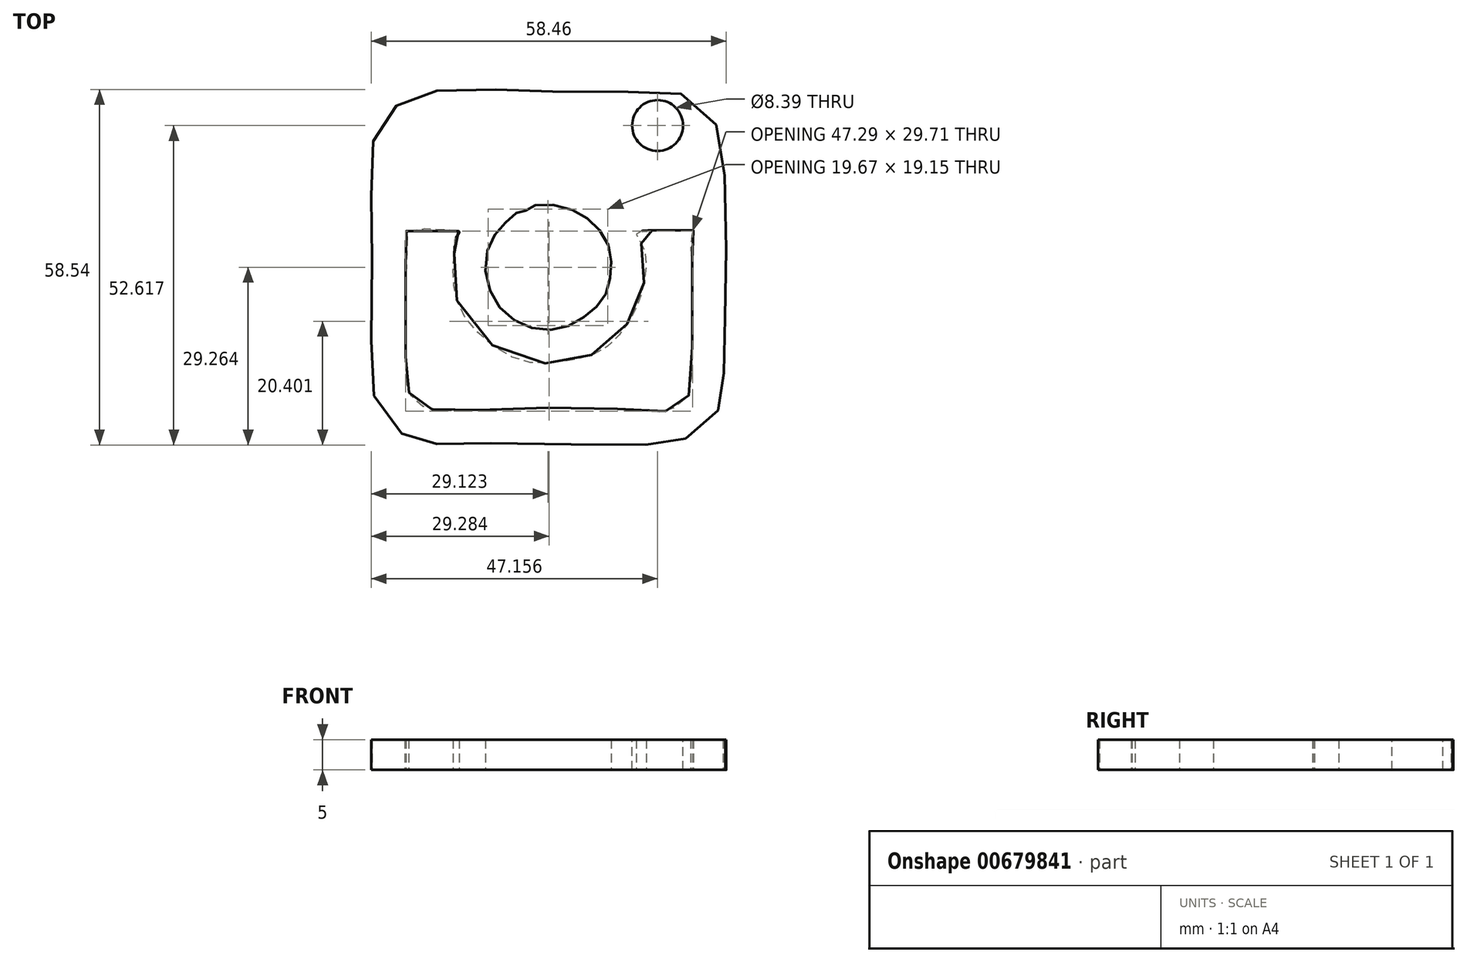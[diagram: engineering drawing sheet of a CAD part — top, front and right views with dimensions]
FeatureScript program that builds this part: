
annotation { "Feature Type Name" : "Feature", "Feature Type Description" : "" }
export const myFeature = defineFeature(function(context is Context, id is Id, definition is map)
    precondition{}
    {
        {
            var Q0;
            Q0=qCreatedBy(makeId("Top.planeOp"),FACE);
            var sketch = newSketch(context, id + "F0", { "sketchPlane" : qUnion([Q0])});
            skFitSpline(sketch, "E0", {"points": [v(-41.99, 61.02) * mm, v(-51.6, 60.82) * mm, v(-56.45, 59.73) * mm, v(-61, 55.57) * mm, v(-62.29, 51.5) * mm, v(-62.49, 42.4) * mm, v(-62.39, 30.61) * mm, v(-62.49, 14.08) * mm, v(-61.6, 9.52) * mm, v(-57.44, 4.37) * mm, v(-53.87, 2.79) * mm, v(-49.71, 2.69) * mm, v(-38.62, 2.79) * mm, v(-20.4, 2.5) * mm, v(-12.88, 2.89) * mm, v(-10.2, 3.88) * mm, v(-6.04, 7.34) * mm, v(-4.26, 11.6) * mm, v(-4.56, 15.56) * mm, v(-4.16, 25.47) * mm, v(-4.16, 38.93) * mm, v(-4.75, 52) * mm, v(-6.44, 56.26) * mm, v(-11.49, 60.32) * mm, v(-18.32, 60.72) * mm, v(-33.37, 60.72) * mm, v(-41.99, 61.02) * mm]});
            skFitSpline(sketch, "E1", {"points": [v(-37.14, 41.11) * mm, v(-38.42, 40.81) * mm, v(-40.8, 38.74) * mm, v(-43.18, 35.27) * mm, v(-43.38, 29.23) * mm, v(-40.5, 24.28) * mm, v(-35.65, 21.7) * mm, v(-30.4, 22) * mm, v(-26.44, 24.38) * mm, v(-23.97, 27.25) * mm, v(-23.07, 31.3) * mm, v(-23.47, 35.37) * mm, v(-26.14, 39.13) * mm, v(-30, 41.4) * mm, v(-35.45, 42) * mm, v(-37.14, 41.11) * mm]});
            skFitSpline(sketch, "E2", {"points": [v(-48.13, 37.74) * mm, v(-56.74, 37.74) * mm, v(-56.55, 37.55) * mm, v(-56.74, 33.59) * mm, v(-56.74, 13.68) * mm, v(-56.55, 11.8) * mm, v(-55.56, 10.12) * mm, v(-53.38, 8.63) * mm, v(-49.32, 8.14) * mm, v(-37.14, 8.53) * mm, v(-21.99, 8.43) * mm, v(-14.36, 8.04) * mm, v(-12.68, 8.63) * mm, v(-10.3, 10.61) * mm, v(-9.8, 13.38) * mm, v(-9.7, 33.39) * mm, v(-9.8, 37.25) * mm, v(-9.5, 37.84) * mm, v(-12.08, 37.84) * mm, v(-18.72, 37.55) * mm, v(-18.82, 36.95) * mm, v(-17.53, 34.67) * mm, v(-17.63, 29.23) * mm, v(-19.6, 23.68) * mm, v(-24.36, 18.24) * mm, v(-30.4, 16.35) * mm, v(-38.23, 16.55) * mm, v(-47.14, 23.68) * mm, v(-49.02, 30.61) * mm, v(-48.72, 35.86) * mm, v(-48.52, 36.75) * mm, v(-48.13, 37.74) * mm]});
            skSolve(sketch);
        }
        {
            var Q0;
            Q0 = qSketchRegion(id + "F0", true);
            extrude(context, id + "F1", {"entities" : qUnion([Q0]), "depth" : 5 * mm, "offsetDistance" : 25 * mm});
        }
        {
            var Q0;
            Q0=makeQuery(id+"F1.opExtrude","CAP_FACE",FACE,{"disambiguationData":[OSD([sQuery(id+"F0.wireOp",EDGE,"E0"),sQuery(id+"F0.wireOp",EDGE,"E1"),sQuery(id+"F0.wireOp",EDGE,"E2")])],"isStart":false});
            var sketch = newSketch(context, id + "F2", { "sketchPlane" : qUnion([Q0])});
            skCircle(sketch, "E3", {"center": v(-15.36, 55.1) * mm, "radius": 4.2 * mm});
            skSolve(sketch);
        }
        {
            var Q0;
            Q0 = qSketchRegion(id + "F2", true);
            extrude(context, id + "F3", {"entities" : qUnion([Q0]), "operationType" : NewBodyOperationType.REMOVE, "oppositeDirection" : true, "depth" : 5 * mm, "offsetDistance" : 25 * mm});
        }
    });
